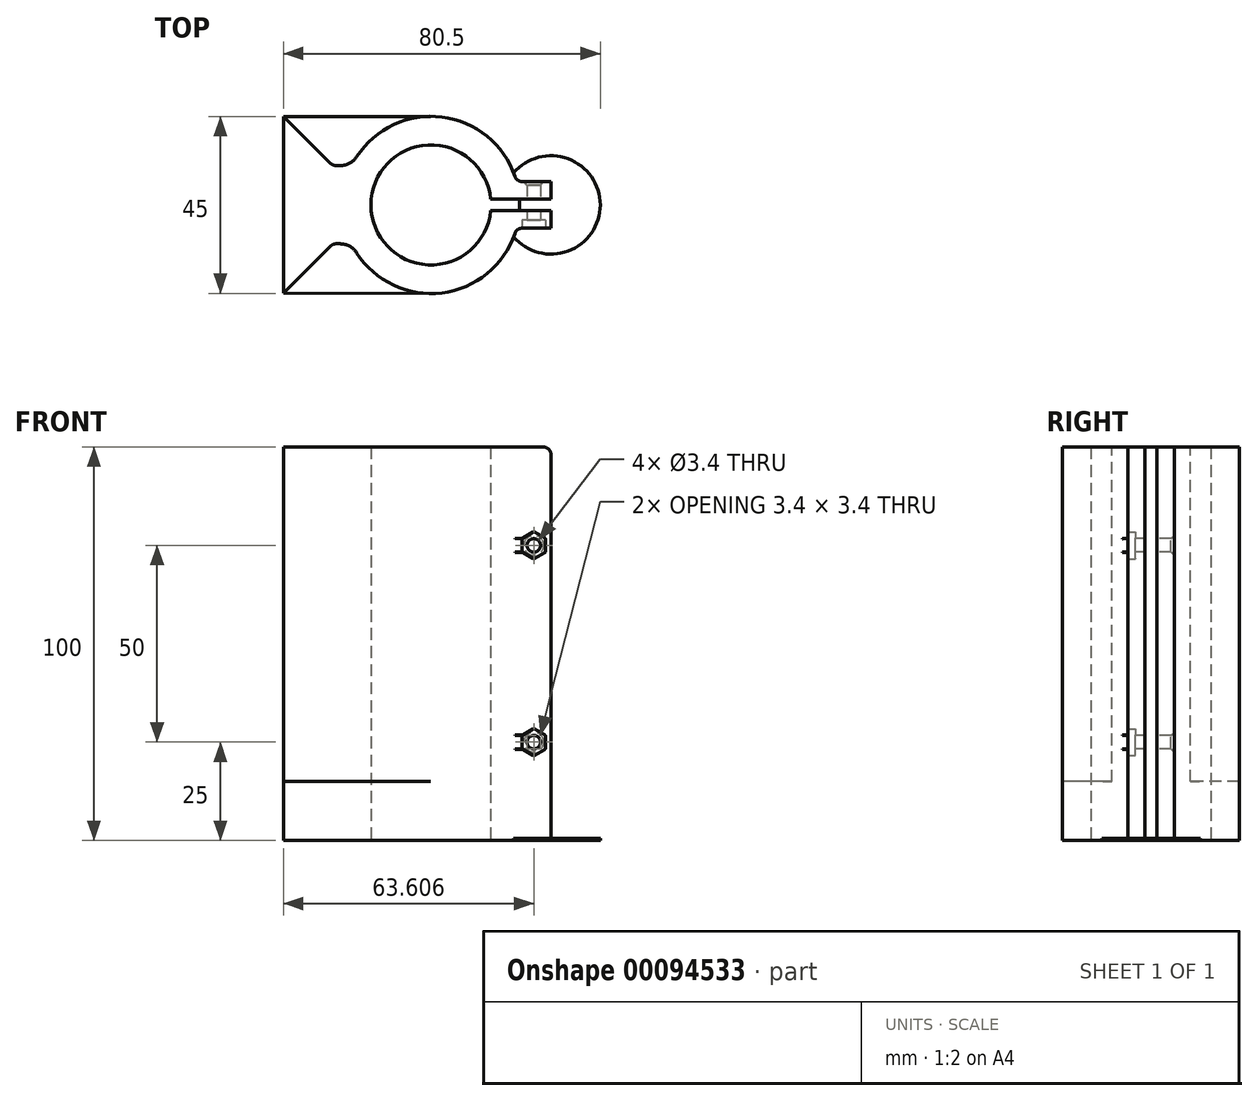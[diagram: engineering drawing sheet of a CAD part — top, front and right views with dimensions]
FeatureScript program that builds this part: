
annotation { "Feature Type Name" : "Feature", "Feature Type Description" : "" }
export const myFeature = defineFeature(function(context is Context, id is Id, definition is map)
    precondition{}
    {
        {
            var Q0;
            Q0=qCreatedBy(makeId("Top.planeOp"),FACE);
            var sketch = newSketch(context, id + "F6", { "sketchPlane" : qUnion([Q0])});
            skCircle(sketch, "E0", {"center": v(0, 0) * mm, "radius": 15.25 * mm});
            skCircle(sketch, "E1", {"center": v(0, 0) * mm, "radius": 22.5 * mm});
            skLineSegment(sketch, "E2", {"start": v(0, 0) * mm, "end": v(-37.5, 0) * mm, "construction": true});
            skLineSegment(sketch, "E3", {"start": v(-24.96, -9.88) * mm, "end": v(-37.5, -22.4) * mm});
            skLineSegment(sketch, "E4", {"start": v(-37.5, -22.4) * mm, "end": v(-37.5, 22.4) * mm});
            skLineSegment(sketch, "E5", {"start": v(-37.5, 22.4) * mm, "end": v(-24.9, 9.99) * mm});
            skLineSegment(sketch, "E6", {"start": v(0, 0) * mm, "end": v(30.5, 0) * mm, "construction": true});
            skLineSegment(sketch, "E7", {"start": v(15.18, 1.5) * mm, "end": v(30.5, 1.5) * mm});
            skLineSegment(sketch, "E8", {"start": v(30.5, 1.5) * mm, "end": v(30.5, 5.9) * mm});
            skLineSegment(sketch, "E9", {"start": v(30.5, 5.9) * mm, "end": v(21.71, 5.9) * mm});
            skLineSegment(sketch, "E10", {"start": v(15.18, -1.5) * mm, "end": v(30.5, -1.5) * mm});
            skLineSegment(sketch, "E11", {"start": v(30.5, -1.5) * mm, "end": v(30.5, -5.9) * mm});
            skLineSegment(sketch, "E12", {"start": v(30.5, -5.9) * mm, "end": v(21.71, -5.9) * mm});
            skLineSegment(sketch, "E13", {"start": v(30.5, 1.5) * mm, "end": v(30.5, -1.5) * mm, "construction": true});
            skLineSegment(sketch, "E14", {"start": v(-24.96, -9.88) * mm, "end": v(-20.22, -9.88) * mm});
            skLineSegment(sketch, "E15", {"start": v(-20.22, -9.88) * mm, "end": v(-20.22, 9.99) * mm});
            skLineSegment(sketch, "E16", {"start": v(-20.22, 9.99) * mm, "end": v(-24.9, 9.99) * mm});
            skLineSegment(sketch, "E17", {"start": v(-37.5, 22.4) * mm, "end": v(0, 22.5) * mm});
            skLineSegment(sketch, "E18", {"start": v(-37.5, -22.4) * mm, "end": v(0, -22.5) * mm});
            skCircle(sketch, "E19", {"center": v(30.5, 0) * mm, "radius": 12.5 * mm});
            skSolve(sketch);
        }
        {
            var Q0;
            {var subQ0=sQuery(id+"F6.wireOp",EDGE,"E3");Q0=makeQuery(id+"F6.imprint","IMPRINT",FACE,{"disambiguationData":[TD([[makeQuery(id+"F6.imprint","IMPRINT",EDGE,{"derivedFrom":subQ0}),-1.0]])]});}
            var Q1;
            {var subQ4=sQuery(id+"F6.wireOp",EDGE,"E8");Q1=makeQuery(id+"F6.imprint","IMPRINT",FACE,{"disambiguationData":[TD([[makeQuery(id+"F6.imprint","IMPRINT",EDGE,{"derivedFrom":subQ4}),1.0]])]});}
            var Q2;
            {var subQ4=sQuery(id+"F6.wireOp",EDGE,"E11");Q2=makeQuery(id+"F6.imprint","IMPRINT",FACE,{"disambiguationData":[TD([[makeQuery(id+"F6.imprint","IMPRINT",EDGE,{"derivedFrom":subQ4}),-1.0]])]});}
            var Q3;
            {var subQ0=sQuery(id+"F6.wireOp",EDGE,"2V47TzDL-QyIf-Jqfv-XyGD-IBXASAq6mVxi");var subQ1=sQuery(id+"F6.wireOp",EDGE,"E1");var subQ3=makeQuery(id+"F6.imprint","INTERSECT",VERTEX,{"derivedFrom":[subQ1,subQ0]});Q3=makeQuery(id+"F6.imprint","IMPRINT",FACE,{"disambiguationData":[TD([[makeQuery(id+"F6.imprint","IMPRINT",EDGE,{"disambiguationData":[TD([[subQ3,-1.0]])],"derivedFrom":subQ1}),1.0]])]});}
            var Q4;
            {var subQ7=sQuery(id+"F6.wireOp",EDGE,"E7");var subQ10=sQuery(id+"F6.wireOp",EDGE,"E0");var subQ11=makeQuery(id+"F6.imprint","INTERSECT",VERTEX,{"derivedFrom":[subQ10,subQ7]});Q4=makeQuery(id+"F6.imprint","IMPRINT",FACE,{"disambiguationData":[TD([[makeQuery(id+"F6.imprint","IMPRINT",EDGE,{"disambiguationData":[TD([[subQ11,-1.0]])],"derivedFrom":subQ10}),-1.0]])]});}
            var Q5;
            {var subQ0=sQuery(id+"F6.wireOp",EDGE,"LleeLQah-G3eV-FA8x-DEfq-08nUu0ICUGUe");var subQ1=sQuery(id+"F6.wireOp",EDGE,"E1");var subQ3=makeQuery(id+"F6.imprint","INTERSECT",VERTEX,{"derivedFrom":[subQ1,subQ0]});Q5=makeQuery(id+"F6.imprint","IMPRINT",FACE,{"disambiguationData":[TD([[makeQuery(id+"F6.imprint","IMPRINT",EDGE,{"disambiguationData":[TD([[subQ3,1.0]])],"derivedFrom":subQ1}),1.0]])]});}
            var Q6;
            {var subQ0=sQuery(id+"F6.wireOp",EDGE,"E15");var subQ1=sQuery(id+"F6.wireOp",EDGE,"E1");var subQ3=makeQuery(id+"F6.imprint","INTERSECT",VERTEX,{"derivedFrom":[subQ1,subQ0]});Q6=makeQuery(id+"F6.imprint","IMPRINT",FACE,{"disambiguationData":[TD([[makeQuery(id+"F6.imprint","IMPRINT",EDGE,{"disambiguationData":[TD([[subQ3,-1.0]])],"derivedFrom":subQ1}),1.0]])]});}
            extrude(context, id + "F0", {"entities" : qUnion([Q0, Q1, Q2, Q3, Q4, Q5, Q6]), "depth" : 100 * mm});
        }
        {
            var Q0;
            Q0=makeQuery(id+"F0.opExtrude","SWEPT_FACE",FACE,{"disambiguationData":[OSD([sQuery(id+"F6.wireOp",EDGE,"E12")])]});
            var sketch = newSketch(context, id + "F7", { "sketchPlane" : qUnion([Q0])});
            skLineSegment(sketch, "E20", {"start": v(26.1, 100) * mm, "end": v(26.1, 50) * mm, "construction": true});
            skLineSegment(sketch, "E21", {"start": v(26.1, 50) * mm, "end": v(26.1, 0) * mm, "construction": true});
            skCircle(sketch, "E22.cCircle", {"center": v(26.1, 75) * mm, "radius": 3 * mm, "construction": true});
            skLineSegment(sketch, "E22.0", {"start": v(23.1, 73.27) * mm, "end": v(23.1, 76.73) * mm});
            skLineSegment(sketch, "E22.1", {"start": v(23.1, 76.73) * mm, "end": v(26.1, 78.46) * mm});
            skLineSegment(sketch, "E22.2", {"start": v(26.1, 78.46) * mm, "end": v(29.1, 76.73) * mm});
            skLineSegment(sketch, "E22.3", {"start": v(29.1, 76.73) * mm, "end": v(29.1, 73.27) * mm});
            skLineSegment(sketch, "E22.4", {"start": v(29.1, 73.27) * mm, "end": v(26.1, 71.54) * mm});
            skLineSegment(sketch, "E22.5", {"start": v(26.1, 71.54) * mm, "end": v(23.1, 73.27) * mm});
            skPoint(sketch, "E22.0.midPoint", {"position": v(23.1, 75) * mm});
            skCircle(sketch, "E23.cCircle", {"center": v(26.1, 25) * mm, "radius": 3 * mm, "construction": true});
            skLineSegment(sketch, "E23.0", {"start": v(23.1, 23.27) * mm, "end": v(23.1, 26.73) * mm});
            skLineSegment(sketch, "E23.1", {"start": v(23.1, 26.73) * mm, "end": v(26.1, 28.46) * mm});
            skLineSegment(sketch, "E23.2", {"start": v(26.1, 28.46) * mm, "end": v(29.1, 26.73) * mm});
            skLineSegment(sketch, "E23.3", {"start": v(29.1, 26.73) * mm, "end": v(29.1, 23.27) * mm});
            skLineSegment(sketch, "E23.4", {"start": v(29.1, 23.27) * mm, "end": v(26.1, 21.54) * mm});
            skLineSegment(sketch, "E23.5", {"start": v(26.1, 21.54) * mm, "end": v(23.1, 23.27) * mm});
            skPoint(sketch, "E23.0.midPoint", {"position": v(23.1, 25) * mm});
            skCircle(sketch, "E24", {"center": v(26.1, 75) * mm, "radius": 1.7 * mm});
            skCircle(sketch, "E25", {"center": v(26.1, 25) * mm, "radius": 1.7 * mm});
            skSolve(sketch);
        }
        {
            var Q0;
            Q0=makeQuery(id+"F7.imprint","IMPRINT",FACE,{"disambiguationData":[TD([[makeQuery(id+"F7.imprint","IMPRINT",EDGE,{"derivedFrom":sQuery(id+"F7.wireOp",EDGE,"E24")}),1.0]])]});
            var Q1;
            Q1=makeQuery(id+"F7.imprint","IMPRINT",FACE,{"disambiguationData":[TD([[makeQuery(id+"F7.imprint","IMPRINT",EDGE,{"derivedFrom":sQuery(id+"F7.wireOp",EDGE,"E25")}),1.0]])]});
            extrude(context, id + "F8", {"entities" : qUnion([Q0, Q1]), "operationType" : NewBodyOperationType.REMOVE, "endBound" : BoundingType.THROUGH_ALL, "oppositeDirection" : true, "depth" : 25 * mm});
        }
        {
            var Q0;
            Q0=makeQuery(id+"F7.imprint","IMPRINT",FACE,{"disambiguationData":[TD([[makeQuery(id+"F7.imprint","IMPRINT",EDGE,{"derivedFrom":sQuery(id+"F7.wireOp",EDGE,"E22.0")}),-1.0]])]});
            var Q1;
            Q1=makeQuery(id+"F7.imprint","IMPRINT",FACE,{"disambiguationData":[TD([[makeQuery(id+"F7.imprint","IMPRINT",EDGE,{"derivedFrom":sQuery(id+"F7.wireOp",EDGE,"E23.0")}),-1.0]])]});
            extrude(context, id + "F9", {"entities" : qUnion([Q0, Q1]), "operationType" : NewBodyOperationType.REMOVE, "oppositeDirection" : true, "depth" : 2 * mm});
        }
        {
            var Q0;
            Q0=makeQuery(id+"F0.opExtrude","CAP_EDGE",EDGE,{"disambiguationData":[OSD([sQuery(id+"F6.wireOp",EDGE,"E11")])],"isStart":false});
            var Q1;
            Q1=makeQuery(id+"F0.opExtrude","CAP_EDGE",EDGE,{"disambiguationData":[OSD([sQuery(id+"F6.wireOp",EDGE,"E8")])],"isStart":false});
            fillet(context, id + "F10", {"entities" : qUnion([Q0, Q1]), "radius" : 2 * mm, "tangentPropagation" : true, "allowEdgeOverflow" : false});
        }
        {
            var Q0;
            Q0=makeQuery(id+"F0.opExtrude","SWEPT_EDGE",EDGE,{"disambiguationData":[OSD([sQuery(id+"F6.wireOp",EDGE,"E1"),sQuery(id+"F6.wireOp",EDGE,"E3")])]});
            var Q1;
            Q1=makeQuery(id+"F0.opExtrude","SWEPT_EDGE",EDGE,{"disambiguationData":[OSD([sQuery(id+"F6.wireOp",EDGE,"E1"),sQuery(id+"F6.wireOp",EDGE,"E5")])]});
            var Q2;
            Q2=makeQuery(id+"F0.opExtrude","SWEPT_EDGE",EDGE,{"disambiguationData":[OSD([sQuery(id+"F6.wireOp",EDGE,"E1"),sQuery(id+"F6.wireOp",EDGE,"E9")])]});
            var Q3;
            Q3=makeQuery(id+"F0.opExtrude","SWEPT_EDGE",EDGE,{"disambiguationData":[OSD([sQuery(id+"F6.wireOp",EDGE,"E1"),sQuery(id+"F6.wireOp",EDGE,"E12")])]});
            fillet(context, id + "F1", {"entities" : qUnion([Q0, Q1, Q2, Q3]), "radius" : 2 * mm, "tangentPropagation" : true, "allowEdgeOverflow" : false});
        }
        {
            var Q0;
            Q0=makeQuery(id+"F9.boolean.opBoolean","COPY",EDGE,{"derivedFrom":makeQuery(id+"F9.opExtrude","SWEPT_EDGE",EDGE,{"disambiguationData":[OSD([sQuery(id+"F7.wireOp",EDGE,"E22.0"),sQuery(id+"F7.wireOp",EDGE,"E22.1")])]})});
            var Q1;
            Q1=makeQuery(id+"F9.boolean.opBoolean","COPY",EDGE,{"derivedFrom":makeQuery(id+"F9.opExtrude","SWEPT_EDGE",EDGE,{"disambiguationData":[OSD([sQuery(id+"F7.wireOp",EDGE,"E22.1"),sQuery(id+"F7.wireOp",EDGE,"E22.2")])]})});
            var Q2;
            Q2=makeQuery(id+"F9.boolean.opBoolean","COPY",EDGE,{"derivedFrom":makeQuery(id+"F9.opExtrude","SWEPT_EDGE",EDGE,{"disambiguationData":[OSD([sQuery(id+"F7.wireOp",EDGE,"E22.0"),sQuery(id+"F7.wireOp",EDGE,"E22.5")])]})});
            var Q3;
            Q3=makeQuery(id+"F9.boolean.opBoolean","COPY",EDGE,{"derivedFrom":makeQuery(id+"F9.opExtrude","SWEPT_EDGE",EDGE,{"disambiguationData":[OSD([sQuery(id+"F7.wireOp",EDGE,"E22.4"),sQuery(id+"F7.wireOp",EDGE,"E22.5")])]})});
            var Q4;
            Q4=makeQuery(id+"F9.boolean.opBoolean","COPY",EDGE,{"derivedFrom":makeQuery(id+"F9.opExtrude","SWEPT_EDGE",EDGE,{"disambiguationData":[OSD([sQuery(id+"F7.wireOp",EDGE,"E22.3"),sQuery(id+"F7.wireOp",EDGE,"E22.4")])]})});
            var Q5;
            Q5=makeQuery(id+"F9.boolean.opBoolean","COPY",EDGE,{"derivedFrom":makeQuery(id+"F9.opExtrude","SWEPT_EDGE",EDGE,{"disambiguationData":[OSD([sQuery(id+"F7.wireOp",EDGE,"E22.2"),sQuery(id+"F7.wireOp",EDGE,"E22.3")])]})});
            var Q6;
            Q6=makeQuery(id+"F9.boolean.opBoolean","COPY",EDGE,{"derivedFrom":makeQuery(id+"F9.opExtrude","SWEPT_EDGE",EDGE,{"disambiguationData":[OSD([sQuery(id+"F7.wireOp",EDGE,"E23.0"),sQuery(id+"F7.wireOp",EDGE,"E23.5")])]})});
            var Q7;
            Q7=makeQuery(id+"F9.boolean.opBoolean","COPY",EDGE,{"derivedFrom":makeQuery(id+"F9.opExtrude","SWEPT_EDGE",EDGE,{"disambiguationData":[OSD([sQuery(id+"F7.wireOp",EDGE,"E23.0"),sQuery(id+"F7.wireOp",EDGE,"E23.1")])]})});
            var Q8;
            Q8=makeQuery(id+"F9.boolean.opBoolean","COPY",EDGE,{"derivedFrom":makeQuery(id+"F9.opExtrude","SWEPT_EDGE",EDGE,{"disambiguationData":[OSD([sQuery(id+"F7.wireOp",EDGE,"E23.2"),sQuery(id+"F7.wireOp",EDGE,"E23.3")])]})});
            var Q9;
            Q9=makeQuery(id+"F9.boolean.opBoolean","COPY",EDGE,{"derivedFrom":makeQuery(id+"F9.opExtrude","SWEPT_EDGE",EDGE,{"disambiguationData":[OSD([sQuery(id+"F7.wireOp",EDGE,"E23.1"),sQuery(id+"F7.wireOp",EDGE,"E23.2")])]})});
            var Q10;
            Q10=makeQuery(id+"F9.boolean.opBoolean","COPY",EDGE,{"derivedFrom":makeQuery(id+"F9.opExtrude","SWEPT_EDGE",EDGE,{"disambiguationData":[OSD([sQuery(id+"F7.wireOp",EDGE,"E23.4"),sQuery(id+"F7.wireOp",EDGE,"E23.5")])]})});
            var Q11;
            Q11=makeQuery(id+"F9.boolean.opBoolean","COPY",EDGE,{"derivedFrom":makeQuery(id+"F9.opExtrude","SWEPT_EDGE",EDGE,{"disambiguationData":[OSD([sQuery(id+"F7.wireOp",EDGE,"E23.3"),sQuery(id+"F7.wireOp",EDGE,"E23.4")])]})});
            fillet(context, id + "F2", {"entities" : qUnion([Q0, Q1, Q2, Q3, Q4, Q5, Q6, Q7, Q8, Q9, Q10, Q11]), "radius" : 0.4 * mm, "tangentPropagation" : true, "allowEdgeOverflow" : false});
        }
        {
            var Q0;
            Q0=makeQuery(id+"F8.boolean.opBoolean","INTERSECT",EDGE,{"derivedFrom":[makeQuery(id+"F0.opExtrude","SWEPT_FACE",FACE,{"disambiguationData":[OSD([sQuery(id+"F6.wireOp",EDGE,"E9")])]}),makeQuery(id+"F8.opExtrude","SWEPT_FACE",FACE,{"disambiguationData":[OSD([sQuery(id+"F7.wireOp",EDGE,"E24")])]})]});
            var Q1;
            Q1=makeQuery(id+"F8.boolean.opBoolean","INTERSECT",EDGE,{"derivedFrom":[makeQuery(id+"F0.opExtrude","SWEPT_FACE",FACE,{"disambiguationData":[OSD([sQuery(id+"F6.wireOp",EDGE,"E9")])]}),makeQuery(id+"F8.opExtrude","SWEPT_FACE",FACE,{"disambiguationData":[OSD([sQuery(id+"F7.wireOp",EDGE,"E25")])]})]});
            chamfer(context, id + "F11", {"entities" : qUnion([Q0, Q1]), "width" : 0.8 * mm, "tangentPropagation" : true});
        }
        {
            var Q0;
            {var subQ1=sQuery(id+"F6.wireOp",EDGE,"E5");Q0=makeQuery(id+"F6.imprint","IMPRINT",FACE,{"disambiguationData":[TD([[makeQuery(id+"F6.imprint","IMPRINT",EDGE,{"derivedFrom":subQ1}),1.0]])]});}
            var Q1;
            {var subQ1=sQuery(id+"F6.wireOp",EDGE,"E3");Q1=makeQuery(id+"F6.imprint","IMPRINT",FACE,{"disambiguationData":[TD([[makeQuery(id+"F6.imprint","IMPRINT",EDGE,{"derivedFrom":subQ1}),1.0]])]});}
            extrude(context, id + "F3", {"entities" : qUnion([Q0, Q1]), "operationType" : NewBodyOperationType.ADD, "depth" : 15 * mm});
        }
        {
            var Q0;
            Q0=makeQuery(id+"F0.opExtrude","SWEPT_EDGE",EDGE,{"disambiguationData":[OSD([sQuery(id+"F6.wireOp",EDGE,"E1"),sQuery(id+"F6.wireOp",EDGE,"E14"),sQuery(id+"F6.wireOp",EDGE,"E15")])]});
            var Q1;
            Q1=makeQuery(id+"F1.opFillet","BLEND_EDGE",EDGE,{"blendedFrom":[makeQuery(id+"F0.opExtrude","SWEPT_EDGE",EDGE,{"disambiguationData":[OSD([sQuery(id+"F6.wireOp",EDGE,"E1"),sQuery(id+"F6.wireOp",EDGE,"E15")])]}),makeQuery(id+"F0.opExtrude","SWEPT_FACE",FACE,{"disambiguationData":[OSD([sQuery(id+"F6.wireOp",EDGE,"E16")])]})],"blendedInto":[makeQuery(id+"F0.opExtrude","SWEPT_FACE",FACE,{"disambiguationData":[OSD([sQuery(id+"F6.wireOp",EDGE,"E16")])]})]});
            fillet(context, id + "F4", {"entities" : qUnion([Q0, Q1]), "radius" : 5 * mm, "tangentPropagation" : true, "allowEdgeOverflow" : false});
        }
        {
            var Q0;
            {var subQ10=sQuery(id+"F6.wireOp",EDGE,"E8");Q0=makeQuery(id+"F6.imprint","IMPRINT",FACE,{"disambiguationData":[TD([[makeQuery(id+"F6.imprint","IMPRINT",EDGE,{"derivedFrom":subQ10}),-1.0]])]});}
            extrude(context, id + "F5", {"entities" : qUnion([Q0]), "operationType" : NewBodyOperationType.ADD, "depth" : 0.5 * mm});
        }
    });
